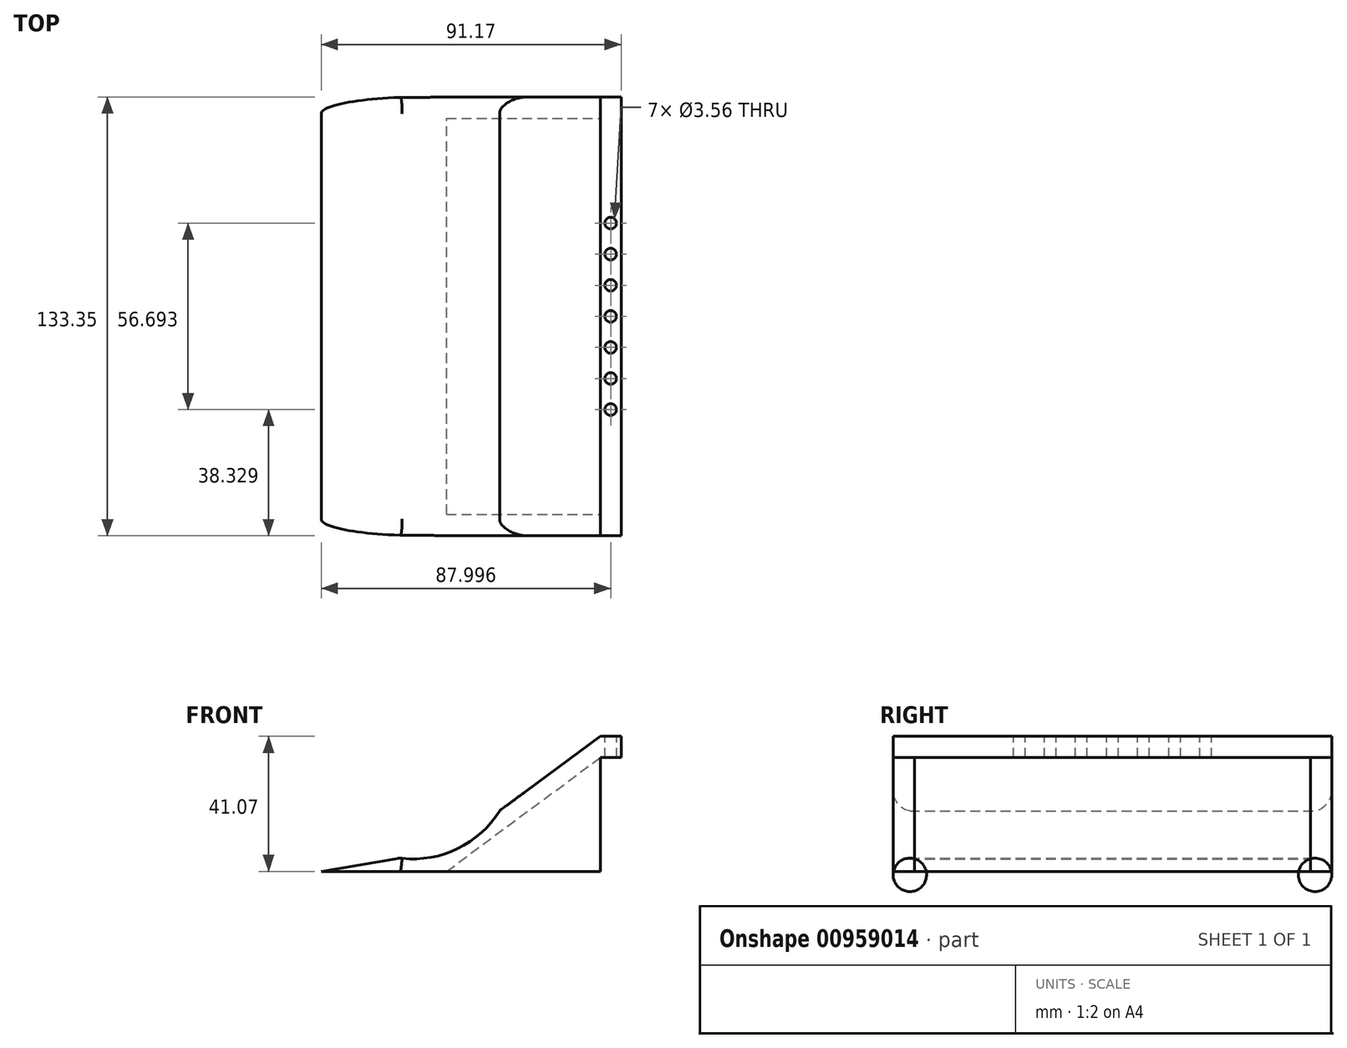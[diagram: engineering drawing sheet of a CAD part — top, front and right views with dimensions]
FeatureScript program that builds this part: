
annotation { "Feature Type Name" : "Feature", "Feature Type Description" : "" }
export const myFeature = defineFeature(function(context is Context, id is Id, definition is map)
    precondition{}
    {
        {
            var Q0;
            Q0=qCreatedBy(makeId("Front.planeOp"),FACE);
            var sketch = newSketch(context, id + "F0", { "sketchPlane" : qUnion([Q0])});
            skLineSegment(sketch, "E0.top", {"start": v(23.36, -17.3) * mm, "end": v(-23.36, -17.3) * mm, "construction": true});
            skLineSegment(sketch, "E0.left", {"start": v(23.36, 17.3) * mm, "end": v(23.36, -17.3) * mm, "construction": true});
            skPoint(sketch, "E0.middle", {"position": v(0, 0) * mm});
            skLineSegment(sketch, "E1", {"start": v(23.36, 17.3) * mm, "end": v(-23.36, -17.3) * mm});
            skLineSegment(sketch, "E2", {"start": v(-23.36, -17.3) * mm, "end": v(-61.46, -17.3) * mm});
            skLineSegment(sketch, "E3", {"start": v(23.36, 23.77) * mm, "end": v(23.36, 17.3) * mm});
            skLineSegment(sketch, "E4", {"start": v(-7.23, 1.12) * mm, "end": v(23.36, 23.77) * mm});
            skLineSegment(sketch, "E5", {"start": v(-61.46, -17.3) * mm, "end": v(-37.53, -13.23) * mm});
            skArc(sketch, "E6", {"start": v(-37.53, -13.23) * mm, "mid": v(-20.26, -10.54) * mm, "end": v(-7.23, 1.12) * mm});
            skPoint(sketch, "E7.orphan", {"position": v(-23.36, -10.82) * mm});
            skSolve(sketch);
        }
        {
            var Q0;
            Q0 = qSketchRegion(id + "F0", true);
            extrude(context, id + "F1", {"entities" : qUnion([Q0]), "depth" : 133.35 * mm, "offsetDistance" : 25.4 * mm});
        }
        {
            var Q0;
            Q0=makeQuery(id+"F1.opExtrude","SWEPT_FACE",FACE,{"disambiguationData":[OSD([sQuery(id+"F0.wireOp",EDGE,"E3")])]});
            var sketch = newSketch(context, id + "F2", { "sketchPlane" : qUnion([Q0])});
            skLineSegment(sketch, "E8.bottom", {"start": v(-133.35, 23.77) * mm, "end": v(-126.87, 23.77) * mm});
            skLineSegment(sketch, "E8.top", {"start": v(-133.35, -17.3) * mm, "end": v(-126.87, -17.3) * mm});
            skLineSegment(sketch, "E8.left", {"start": v(-133.35, 23.77) * mm, "end": v(-133.35, -17.3) * mm});
            skLineSegment(sketch, "E8.right", {"start": v(-126.87, 23.77) * mm, "end": v(-126.87, -17.3) * mm});
            skLineSegment(sketch, "E9", {"start": v(-66.68, 23.77) * mm, "end": v(-66.68, -22.6) * mm});
            skLineSegment(sketch, "E10.MirrorCS", {"start": v(0, -17.3) * mm, "end": v(-6.48, -17.3) * mm});
            skLineSegment(sketch, "E11.MirrorCS", {"start": v(-6.48, 23.77) * mm, "end": v(-6.48, -17.3) * mm});
            skLineSegment(sketch, "E12.MirrorCS", {"start": v(0, 23.77) * mm, "end": v(0, -17.3) * mm});
            skLineSegment(sketch, "E13.MirrorCS", {"start": v(0, 23.77) * mm, "end": v(-6.48, 23.77) * mm});
            skSolve(sketch);
        }
        {
            var Q0;
            {var subQ0=sQuery(id+"F2.wireOp",EDGE,"E8.top");Q0=makeQuery(id+"F2.imprint","IMPRINT",FACE,{"disambiguationData":[TD([[makeQuery(id+"F2.imprint","IMPRINT",EDGE,{"derivedFrom":subQ0}),1.0]])]});}
            var Q1;
            {var subQ0=sQuery(id+"F2.wireOp",EDGE,"E10.MirrorCS");Q1=makeQuery(id+"F2.imprint","IMPRINT",FACE,{"disambiguationData":[TD([[makeQuery(id+"F2.imprint","IMPRINT",EDGE,{"derivedFrom":subQ0}),-1.0]])]});}
            var Q2;
            Q2=makeQuery(id+"F1.opExtrude","SWEPT_BODY",BODY,{"disambiguationData":[OSD([sQuery(id+"F0.wireOp",EDGE,"E1"),sQuery(id+"F0.wireOp",EDGE,"E2"),sQuery(id+"F0.wireOp",EDGE,"E3"),sQuery(id+"F0.wireOp",EDGE,"E4"),sQuery(id+"F0.wireOp",EDGE,"E5")])]});
            extrude(context, id + "F3", {"entities" : qUnion([Q0, Q1]), "operationType" : NewBodyOperationType.ADD, "endBound" : BoundingType.UP_TO_BODY, "oppositeDirection" : true, "depth" : 25.4 * mm, "endBoundEntityBody" : qUnion([Q2]), "offsetDistance" : 25.4 * mm});
        }
        {
            var Q0;
            {var subQ0=sQuery(id+"F0.wireOp",EDGE,"E3");var subQ1=sQuery(id+"F0.wireOp",EDGE,"E1");Q0=makeQuery(id+"F3.boolean.opBoolean","MERGE",FACE,{"derivedFrom":[makeQuery(id+"F1.opExtrude","SWEPT_FACE",FACE,{"disambiguationData":[OSD([subQ0])]}),makeQuery(id+"F3.opExtrude","CAP_FACE",FACE,{"disambiguationData":[OSD([subQ1,subQ0,sQuery(id+"F2.wireOp",EDGE,"E8.top"),sQuery(id+"F2.wireOp",EDGE,"E8.left"),sQuery(id+"F2.wireOp",EDGE,"E8.right")])],"isStart":true}),makeQuery(id+"F3.opExtrude","CAP_FACE",FACE,{"disambiguationData":[OSD([subQ1,subQ0,sQuery(id+"F2.wireOp",EDGE,"E10.MirrorCS"),sQuery(id+"F2.wireOp",EDGE,"E11.MirrorCS"),sQuery(id+"F2.wireOp",EDGE,"E12.MirrorCS")])],"isStart":true})]});}
            var sketch = newSketch(context, id + "F4", { "sketchPlane" : qUnion([Q0])});
            skLineSegment(sketch, "E14.bottom", {"start": v(-133.35, 23.77) * mm, "end": v(0, 23.77) * mm});
            skLineSegment(sketch, "E14.top", {"start": v(-133.35, 17.3) * mm, "end": v(0, 17.3) * mm});
            skLineSegment(sketch, "E14.left", {"start": v(-133.35, 23.77) * mm, "end": v(-133.35, 17.3) * mm});
            skLineSegment(sketch, "E14.right", {"start": v(0, 23.77) * mm, "end": v(0, 17.3) * mm});
            skSolve(sketch);
        }
        {
            var Q0;
            Q0=makeQuery(id+"F4.imprint","IMPRINT",FACE,{"disambiguationData":[TD([[makeQuery(id+"F4.imprint","IMPRINT",EDGE,{"derivedFrom":sQuery(id+"F4.wireOp",EDGE,"E14.bottom")}),-1.0]])]});
            extrude(context, id + "F5", {"entities" : qUnion([Q0]), "operationType" : NewBodyOperationType.ADD, "depth" : 6.35 * mm, "offsetDistance" : 25.4 * mm});
        }
        {
            var Q0;
            Q0=makeQuery(id+"F5.opExtrude","SWEPT_FACE",FACE,{"disambiguationData":[OSD([sQuery(id+"F4.wireOp",EDGE,"E14.bottom")])]});
            var sketch = newSketch(context, id + "F6", { "sketchPlane" : qUnion([Q0])});
            skLineSegment(sketch, "E15", {"start": v(26.54, 0) * mm, "end": v(26.54, -133.35) * mm, "construction": true});
            skCircle(sketch, "E16", {"center": v(26.54, -66.68) * mm, "radius": 1.78 * mm});
            skCircle(sketch, "E17", {"center": v(26.54, -57.23) * mm, "radius": 1.78 * mm});
            skCircle(sketch, "E18", {"center": v(26.54, -47.78) * mm, "radius": 1.78 * mm});
            skCircle(sketch, "E19", {"center": v(26.54, -76.12) * mm, "radius": 1.78 * mm});
            skCircle(sketch, "E20", {"center": v(26.54, -85.57) * mm, "radius": 1.78 * mm});
            skCircle(sketch, "E21", {"center": v(26.54, -38.33) * mm, "radius": 1.78 * mm});
            skCircle(sketch, "E22", {"center": v(26.54, -95.02) * mm, "radius": 1.78 * mm});
            skSolve(sketch);
        }
        {
            var Q0;
            Q0=makeQuery(id+"F6.imprint","IMPRINT",FACE,{"disambiguationData":[TD([[makeQuery(id+"F6.imprint","IMPRINT",EDGE,{"derivedFrom":sQuery(id+"F6.wireOp",EDGE,"E21")}),1.0]])]});
            var Q1;
            Q1=makeQuery(id+"F6.imprint","IMPRINT",FACE,{"disambiguationData":[TD([[makeQuery(id+"F6.imprint","IMPRINT",EDGE,{"derivedFrom":sQuery(id+"F6.wireOp",EDGE,"E18")}),1.0]])]});
            var Q2;
            Q2=makeQuery(id+"F6.imprint","IMPRINT",FACE,{"disambiguationData":[TD([[makeQuery(id+"F6.imprint","IMPRINT",EDGE,{"derivedFrom":sQuery(id+"F6.wireOp",EDGE,"E17")}),1.0]])]});
            var Q3;
            Q3=makeQuery(id+"F6.imprint","IMPRINT",FACE,{"disambiguationData":[TD([[makeQuery(id+"F6.imprint","IMPRINT",EDGE,{"derivedFrom":sQuery(id+"F6.wireOp",EDGE,"E16")}),1.0]])]});
            var Q4;
            Q4=makeQuery(id+"F6.imprint","IMPRINT",FACE,{"disambiguationData":[TD([[makeQuery(id+"F6.imprint","IMPRINT",EDGE,{"derivedFrom":sQuery(id+"F6.wireOp",EDGE,"E19")}),1.0]])]});
            var Q5;
            Q5=makeQuery(id+"F6.imprint","IMPRINT",FACE,{"disambiguationData":[TD([[makeQuery(id+"F6.imprint","IMPRINT",EDGE,{"derivedFrom":sQuery(id+"F6.wireOp",EDGE,"E20")}),1.0]])]});
            var Q6;
            Q6=makeQuery(id+"F6.imprint","IMPRINT",FACE,{"disambiguationData":[TD([[makeQuery(id+"F6.imprint","IMPRINT",EDGE,{"derivedFrom":sQuery(id+"F6.wireOp",EDGE,"E22")}),1.0]])]});
            extrude(context, id + "F7", {"entities" : qUnion([Q0, Q1, Q2, Q3, Q4, Q5, Q6]), "operationType" : NewBodyOperationType.REMOVE, "oppositeDirection" : true, "depth" : 25.4 * mm, "offsetDistance" : 25.4 * mm});
        }
        {
            var Q0;
            Q0=makeQuery(id+"F1.opExtrude","CAP_EDGE",EDGE,{"disambiguationData":[OSD([sQuery(id+"F0.wireOp",EDGE,"E6")])],"isStart":false});
            var Q1;
            Q1=makeQuery(id+"F1.opExtrude","CAP_EDGE",EDGE,{"disambiguationData":[OSD([sQuery(id+"F0.wireOp",EDGE,"E6")])],"isStart":true});
            fillet(context, id + "F8", {"entities" : qUnion([Q0, Q1]), "tangentPropagation" : true, "radius" : 5.08 * mm, "defaultsChanged" : true, "vertexSettings" : [], "allowEdgeOverflow" : false});
        }
        {
            var Q0;
            Q0=makeQuery(id+"F1.opExtrude","SWEPT_EDGE",EDGE,{"disambiguationData":[OSD([sQuery(id+"F0.wireOp",EDGE,"E5"),sQuery(id+"F0.wireOp",EDGE,"E6")])]});
            fillet(context, id + "F9", {"entities" : qUnion([Q0]), "tangentPropagation" : true, "radius" : 5.08 * mm, "defaultsChanged" : true, "vertexSettings" : [], "allowEdgeOverflow" : false});
        }
    });
